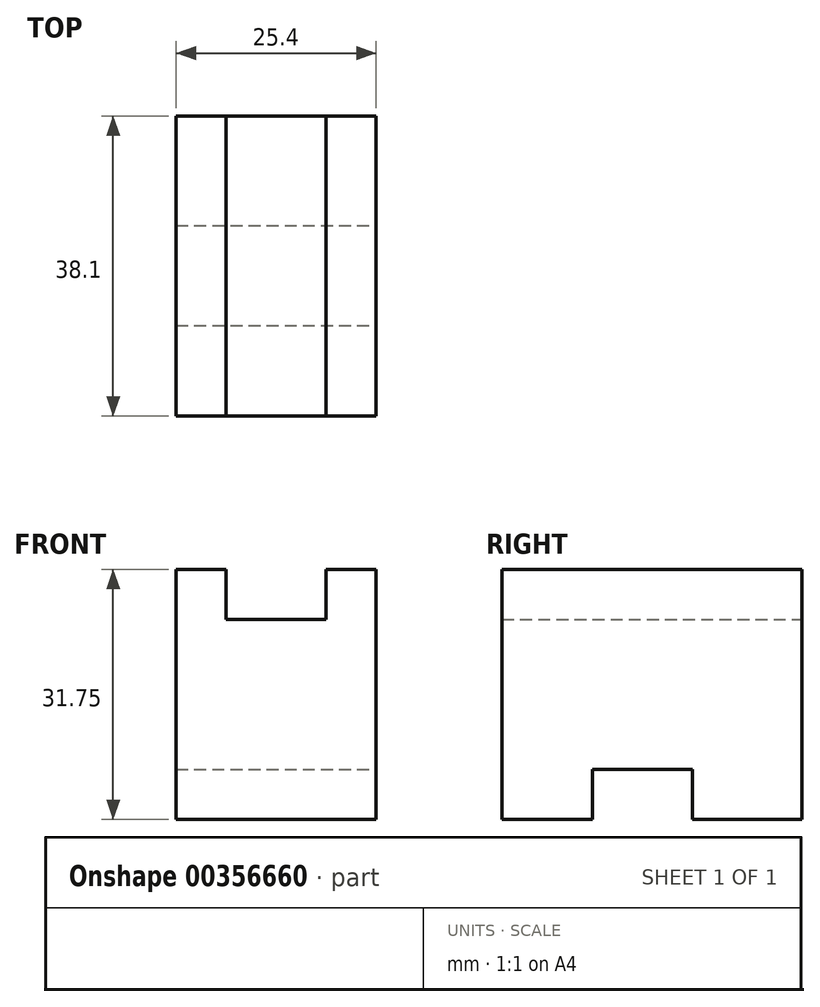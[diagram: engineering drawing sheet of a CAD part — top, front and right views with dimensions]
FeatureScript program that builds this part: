
annotation { "Feature Type Name" : "Feature", "Feature Type Description" : "" }
export const myFeature = defineFeature(function(context is Context, id is Id, definition is map)
    precondition{}
    {
        {
            var Q0;
            Q0=qCreatedBy(makeId("Front.planeOp"),FACE);
            var sketch = newSketch(context, id + "F0", { "sketchPlane" : qUnion([Q0])});
            skLineSegment(sketch, "E0", {"start": v(-6.35, -19.22) * mm, "end": v(19.05, -19.22) * mm});
            skLineSegment(sketch, "E1", {"start": v(19.05, -19.22) * mm, "end": v(19.05, 12.53) * mm});
            skLineSegment(sketch, "E2", {"start": v(19.05, 12.53) * mm, "end": v(12.7, 12.53) * mm});
            skLineSegment(sketch, "E3", {"start": v(12.7, 12.53) * mm, "end": v(12.7, 6.18) * mm});
            skLineSegment(sketch, "E4", {"start": v(12.7, 6.18) * mm, "end": v(0, 6.18) * mm});
            skLineSegment(sketch, "E5", {"start": v(0, 6.18) * mm, "end": v(0, 12.53) * mm});
            skLineSegment(sketch, "E6", {"start": v(0, 12.53) * mm, "end": v(-6.35, 12.53) * mm});
            skLineSegment(sketch, "E7", {"start": v(-6.35, 12.53) * mm, "end": v(-6.35, -19.22) * mm});
            skSolve(sketch);
        }
        {
            var Q0;
            Q0=makeQuery(id+"F0.imprint","IMPRINT",FACE,{"disambiguationData":[TD([[makeQuery(id+"F0.imprint","IMPRINT",EDGE,{"derivedFrom":sQuery(id+"F0.wireOp",EDGE,"E0")}),1.0]])]});
            extrude(context, id + "F1", {"entities" : qUnion([Q0]), "depth" : 38.1 * mm});
        }
        {
            var Q0;
            Q0=makeQuery(id+"F1.opExtrude","SWEPT_FACE",FACE,{"disambiguationData":[OSD([sQuery(id+"F0.wireOp",EDGE,"E1")])]});
            var sketch = newSketch(context, id + "F2", { "sketchPlane" : qUnion([Q0])});
            skLineSegment(sketch, "E8", {"start": v(-26.62, -12.87) * mm, "end": v(-26.62, -19.22) * mm});
            skPoint(sketch, "E8.endSnap0", {"position": v(-19.05, -19.22) * mm});
            skLineSegment(sketch, "E9", {"start": v(-26.62, -12.87) * mm, "end": v(-13.92, -12.87) * mm});
            skLineSegment(sketch, "E10", {"start": v(-13.92, -12.87) * mm, "end": v(-13.92, -19.22) * mm});
            skSolve(sketch);
        }
        {
            var Q0;
            {var subQ0=sQuery(id+"F2.wireOp",EDGE,"E8");Q0=makeQuery(id+"F2.imprint","IMPRINT",FACE,{"disambiguationData":[TD([[makeQuery(id+"F2.imprint","IMPRINT",EDGE,{"derivedFrom":subQ0}),1.0]])]});}
            extrude(context, id + "F3", {"entities" : qUnion([Q0]), "operationType" : NewBodyOperationType.REMOVE, "oppositeDirection" : true, "depth" : 25.4 * mm});
        }
    });
